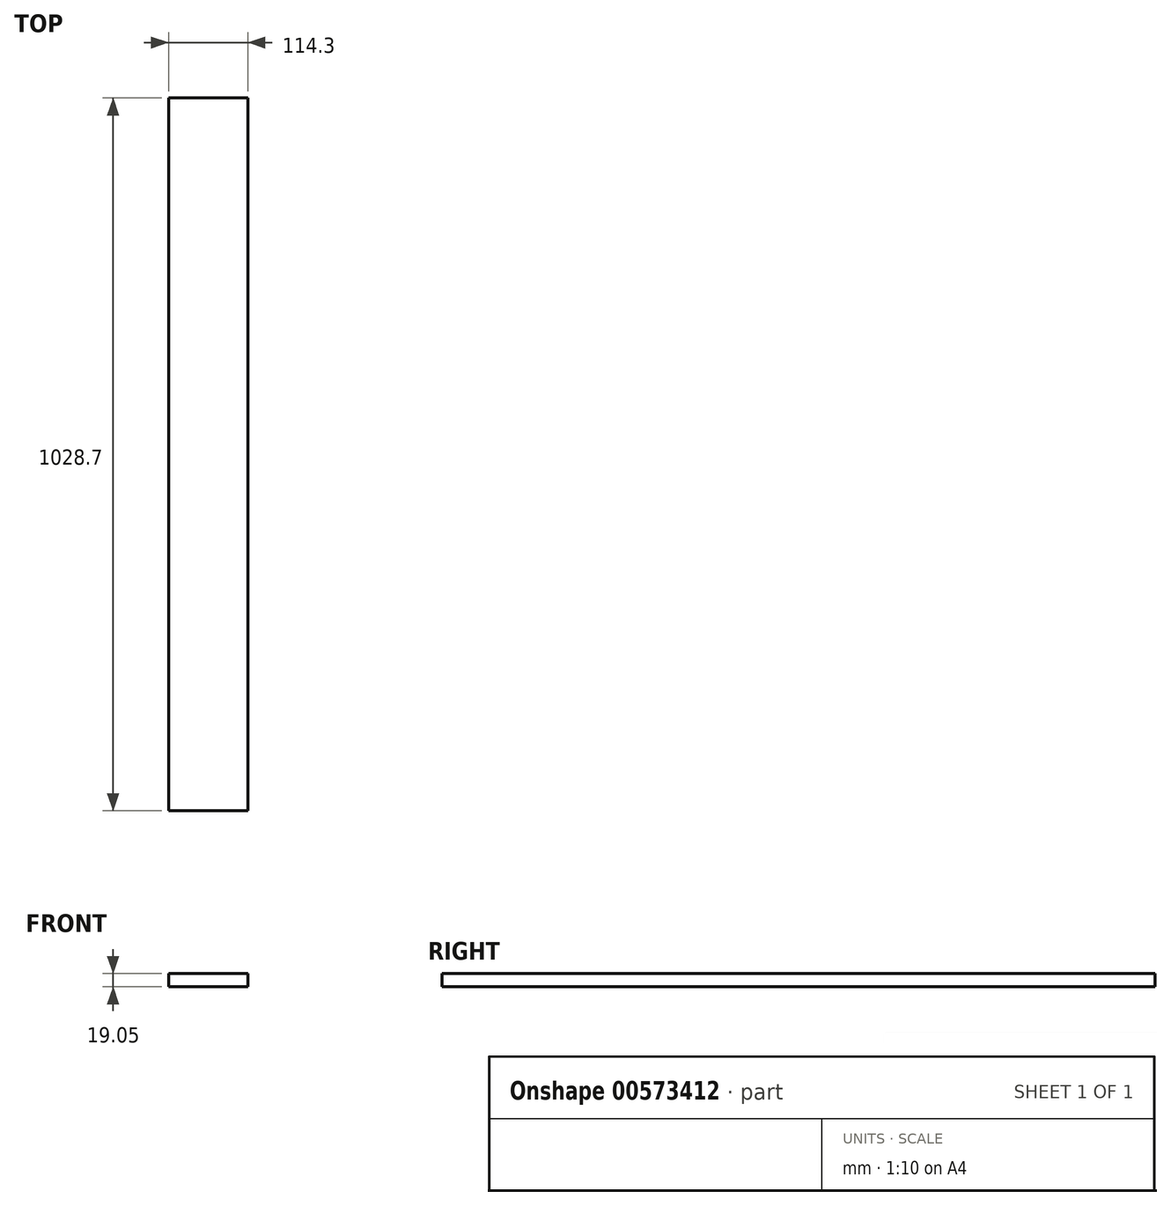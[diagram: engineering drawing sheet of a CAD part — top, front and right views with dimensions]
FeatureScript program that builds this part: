
annotation { "Feature Type Name" : "Feature", "Feature Type Description" : "" }
export const myFeature = defineFeature(function(context is Context, id is Id, definition is map)
    precondition{}
    {
        {
            var Q0;
            Q0=qCreatedBy(makeId("Top.planeOp"),FACE);
            var sketch = newSketch(context, id + "F0", { "sketchPlane" : qUnion([Q0])});
            skLineSegment(sketch, "E0.bottom", {"start": v(57.15, 514.35) * mm, "end": v(-57.15, 514.35) * mm});
            skLineSegment(sketch, "E0.top", {"start": v(57.15, -514.35) * mm, "end": v(-57.15, -514.35) * mm});
            skLineSegment(sketch, "E0.left", {"start": v(57.15, 514.35) * mm, "end": v(57.15, -514.35) * mm});
            skLineSegment(sketch, "E0.right", {"start": v(-57.15, 514.35) * mm, "end": v(-57.15, -514.35) * mm});
            skPoint(sketch, "E0.middle", {"position": v(0, 0) * mm});
            skSolve(sketch);
        }
        {
            var Q0;
            Q0=makeQuery(id+"F0.imprint","IMPRINT",FACE,{"disambiguationData":[TD([[makeQuery(id+"F0.imprint","IMPRINT",EDGE,{"derivedFrom":sQuery(id+"F0.wireOp",EDGE,"E0.bottom")}),1.0]])]});
            extrude(context, id + "F1", {"entities" : qUnion([Q0]), "depth" : 19.05 * mm, "offsetDistance" : 25.4 * mm});
        }
    });
